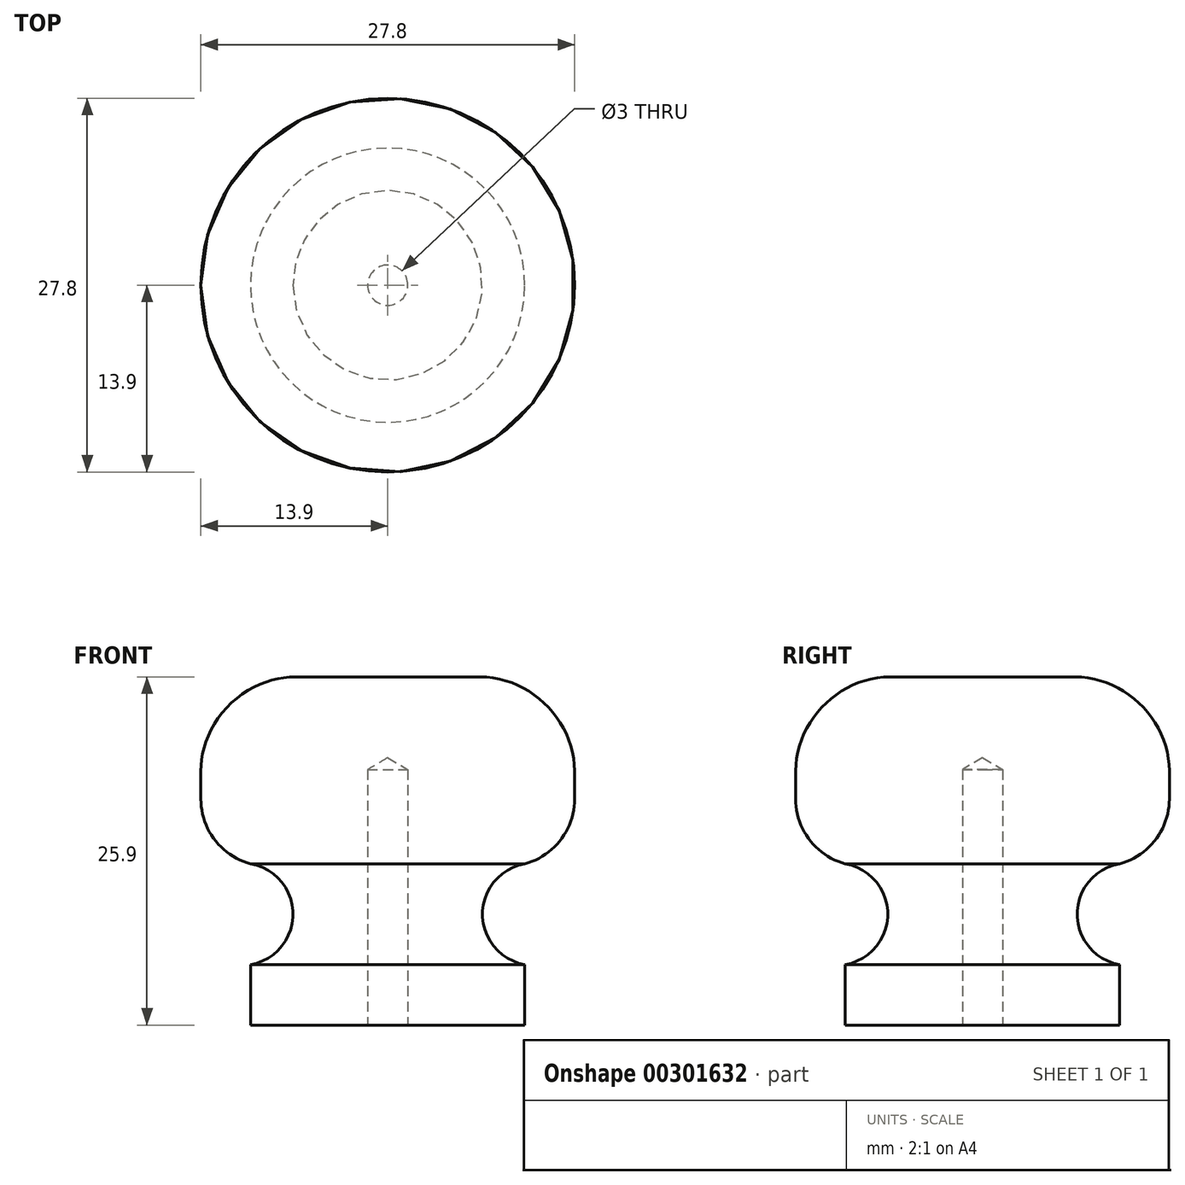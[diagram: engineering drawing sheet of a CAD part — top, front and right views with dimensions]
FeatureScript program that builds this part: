
annotation { "Feature Type Name" : "Feature", "Feature Type Description" : "" }
export const myFeature = defineFeature(function(context is Context, id is Id, definition is map)
    precondition{}
    {
        {
            var Q0;
            Q0=qCreatedBy(makeId("Front.planeOp"),FACE);
            var sketch = newSketch(context, id + "F0", { "sketchPlane" : qUnion([Q0])});
            skLineSegment(sketch, "E0", {"start": v(0, 0) * mm, "end": v(10.2, 0) * mm});
            skLineSegment(sketch, "E1", {"start": v(10.2, 0) * mm, "end": v(10.2, 4.5) * mm});
            skArc(sketch, "E2", {"start": v(10.2, 12) * mm, "mid": v(7.05, 8.25) * mm, "end": v(10.2, 4.5) * mm});
            skLineSegment(sketch, "E3", {"start": v(0, 0) * mm, "end": v(0, 25.9) * mm});
            skLineSegment(sketch, "E4", {"start": v(10.2, 12) * mm, "end": v(13.9, 12) * mm});
            skLineSegment(sketch, "E5", {"start": v(13.9, 12) * mm, "end": v(13.9, 25.9) * mm});
            skLineSegment(sketch, "E6", {"start": v(13.9, 25.9) * mm, "end": v(0, 25.9) * mm});
            skPoint(sketch, "E7", {"position": v(0, 0) * mm});
            skSolve(sketch);
        }
        {
            var Q0;
            Q0 = qSketchRegion(id + "F0", true);
            var Q1;
            Q1=sQuery(id+"F0.wireOp",EDGE,"E3");
            revolve(context, id + "F1", {"entities" : qUnion([Q0]), "axis" : qUnion([Q1]), "revolveType" : RevolveType.FULL});
        }
        {
            var Q0;
            Q0=makeQuery(id+"F1.opRevolve","SWEPT_EDGE",EDGE,{"disambiguationData":[OSD([sQuery(id+"F0.wireOp",EDGE,"E4"),sQuery(id+"F0.wireOp",EDGE,"E5")])]});
            fillet(context, id + "F2", {"entities" : qUnion([Q0]), "radius" : 5 * mm, "tangentPropagation" : true, "allowEdgeOverflow" : false});
        }
        {
            var Q0;
            Q0=makeQuery(id+"F1.opRevolve","SWEPT_EDGE",EDGE,{"disambiguationData":[OSD([sQuery(id+"F0.wireOp",EDGE,"E5"),sQuery(id+"F0.wireOp",EDGE,"E6")])]});
            fillet(context, id + "F3", {"entities" : qUnion([Q0]), "radius" : 7 * mm, "tangentPropagation" : true, "rho" : 0.4, "crossSection" : FilletCrossSection.CONIC, "allowEdgeOverflow" : false});
        }
        {
            var Q0;
            Q0=makeQuery(id+"F1.opRevolve","SWEPT_FACE",FACE,{"disambiguationData":[OSD([sQuery(id+"F0.wireOp",EDGE,"E0")])]});
            var sketch = newSketch(context, id + "F4", { "sketchPlane" : qUnion([Q0])});
            skPoint(sketch, "E8", {"position": v(0, 0) * mm});
            skSolve(sketch);
        }
        {
            var Q0;
            Q0=sQuery(id+"F4.wireOp",VERTEX,"E8");
            var Q1;
            Q1=makeQuery(id+"F1.opRevolve","SWEPT_BODY",BODY,{"disambiguationData":[OSD([sQuery(id+"F0.wireOp",EDGE,"E0"),sQuery(id+"F0.wireOp",EDGE,"E1"),sQuery(id+"F0.wireOp",EDGE,"E2"),sQuery(id+"F0.wireOp",EDGE,"E3"),sQuery(id+"F0.wireOp",EDGE,"E4"),sQuery(id+"F0.wireOp",EDGE,"E5"),sQuery(id+"F0.wireOp",EDGE,"E6")])]});
            hole(context, id + "F5", {"style" : HoleStyle.SIMPLE, "endStyle" : HoleEndStyle.BLIND, "holeDiameter" : 3 * mm, "holeDepth" : 19 * mm, "tappedDepth" : 12 * mm, "tapClearance" : 3, "locations" : qUnion([Q0]), "scope" : qUnion([Q1])});
        }
    });
